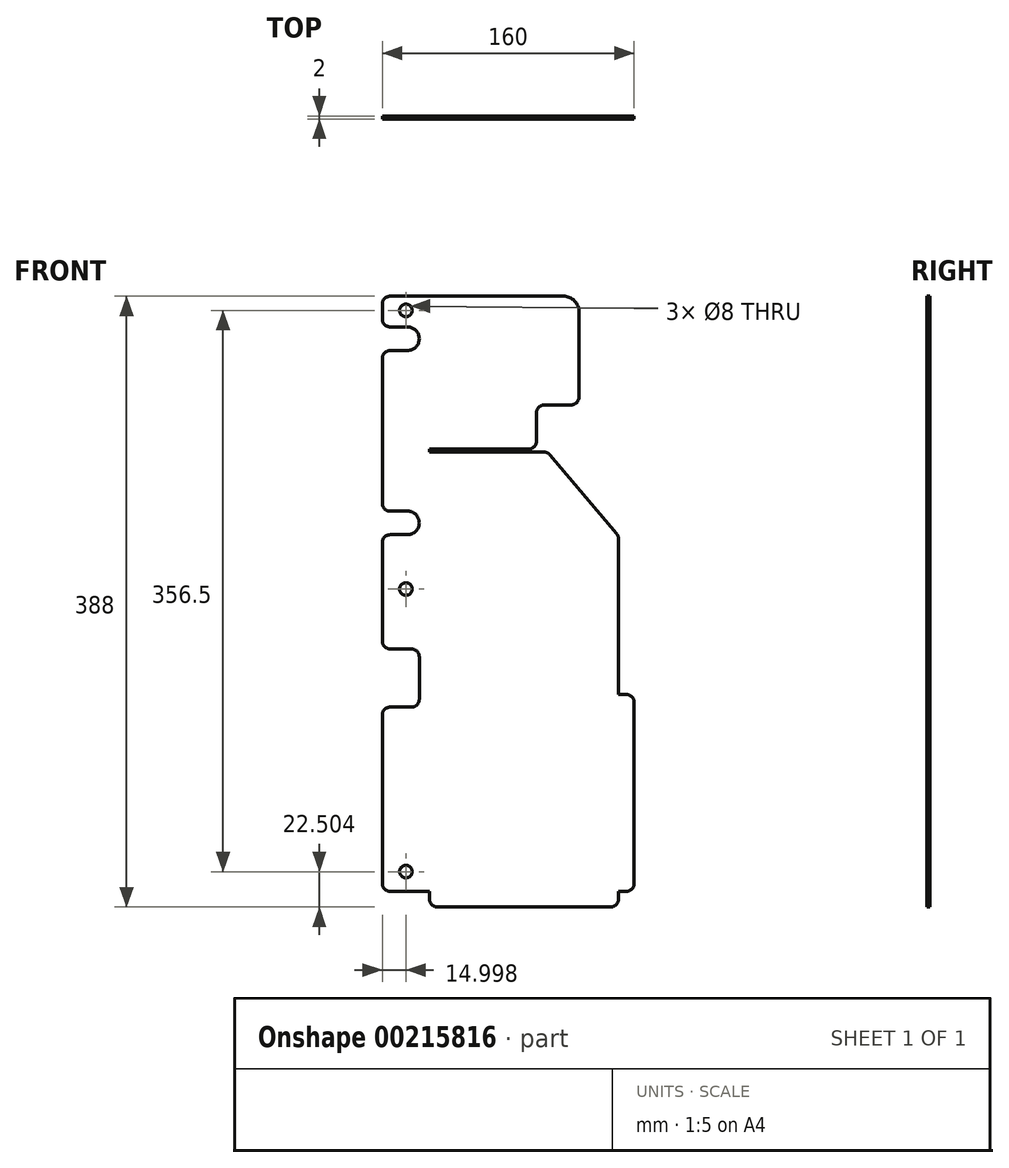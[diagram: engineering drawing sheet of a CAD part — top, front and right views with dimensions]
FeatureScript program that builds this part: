
annotation { "Feature Type Name" : "Feature", "Feature Type Description" : "" }
export const myFeature = defineFeature(function(context is Context, id is Id, definition is map)
    precondition{}
    {
        {
            var Q0;
            Q0=qCreatedBy(makeId("Front.planeOp"),FACE);
            var sketch = newSketch(context, id + "F0", { "sketchPlane" : qUnion([Q0])});
            skLineSegment(sketch, "E0", {"start": v(-23.05, 148.62) * mm, "end": v(56.95, 148.62) * mm});
            skLineSegment(sketch, "E1", {"start": v(66.95, 138.62) * mm, "end": v(66.95, 84.64) * mm});
            skLineSegment(sketch, "E2", {"start": v(61.95, 79.64) * mm, "end": v(44.95, 79.64) * mm});
            skLineSegment(sketch, "E3", {"start": v(39.95, 74.64) * mm, "end": v(39.95, 56.62) * mm});
            skLineSegment(sketch, "E4", {"start": v(34.95, 51.62) * mm, "end": v(-28.05, 51.62) * mm});
            skLineSegment(sketch, "E5", {"start": v(-28.05, 49.62) * mm, "end": v(44.63, 49.62) * mm});
            skLineSegment(sketch, "E6", {"start": v(48.45, 47.85) * mm, "end": v(90.76, -2.16) * mm});
            skLineSegment(sketch, "E7", {"start": v(91.95, -5.39) * mm, "end": v(91.95, -229.38) * mm});
            skLineSegment(sketch, "E8", {"start": v(91.95, -229.38) * mm, "end": v(-28.05, -229.38) * mm});
            skLineSegment(sketch, "E9", {"start": v(-28.05, -229.38) * mm, "end": v(-53.05, -229.38) * mm});
            skLineSegment(sketch, "E10", {"start": v(-58.05, -224.38) * mm, "end": v(-58.05, -117.38) * mm});
            skLineSegment(sketch, "E11", {"start": v(-53.05, 148.62) * mm, "end": v(-23.05, 148.62) * mm});
            skLineSegment(sketch, "E12", {"start": v(91.95, -104.38) * mm, "end": v(96.95, -104.38) * mm});
            skLineSegment(sketch, "E13", {"start": v(101.95, -109.38) * mm, "end": v(101.95, -224.38) * mm});
            skLineSegment(sketch, "E14", {"start": v(96.95, -229.38) * mm, "end": v(91.95, -229.38) * mm});
            skLineSegment(sketch, "E15", {"start": v(91.95, -229.38) * mm, "end": v(91.95, -234.38) * mm});
            skLineSegment(sketch, "E16", {"start": v(86.95, -239.38) * mm, "end": v(-23.05, -239.38) * mm});
            skLineSegment(sketch, "E17", {"start": v(-28.05, -234.38) * mm, "end": v(-28.05, -229.38) * mm});
            skLineSegment(sketch, "E18", {"start": v(-53.05, -75.38) * mm, "end": v(-39.55, -75.38) * mm});
            skLineSegment(sketch, "E19", {"start": v(-53.05, -112.38) * mm, "end": v(-39.55, -112.38) * mm});
            skLineSegment(sketch, "E20.trimOffspring", {"start": v(-58.05, -70.38) * mm, "end": v(-58.05, -7.87) * mm});
            skPoint(sketch, "E21.newPointA", {"position": v(-28.05, -75.38) * mm});
            skPoint(sketch, "E21.newPointB", {"position": v(-28.05, 148.62) * mm});
            skPoint(sketch, "E22.newPointA", {"position": v(-28.05, -229.38) * mm});
            skPoint(sketch, "E23.visualSharp", {"position": v(-58.05, -112.38) * mm});
            skArc(sketch, "E23.filletArc", {"start": v(-53.05, -112.38) * mm, "mid": v(-56.59, -113.84) * mm, "end": v(-58.05, -117.38) * mm});
            skPoint(sketch, "E24.visualSharp", {"position": v(-58.05, -75.38) * mm});
            skArc(sketch, "E24.filletArc", {"start": v(-58.05, -70.38) * mm, "mid": v(-56.59, -73.91) * mm, "end": v(-53.05, -75.38) * mm});
            skPoint(sketch, "E25.visualSharp", {"position": v(-58.05, 148.62) * mm});
            skArc(sketch, "E25.filletArc", {"start": v(-53.05, 148.62) * mm, "mid": v(-56.59, 147.16) * mm, "end": v(-58.05, 143.62) * mm});
            skPoint(sketch, "E26.visualSharp", {"position": v(66.95, 148.62) * mm});
            skArc(sketch, "E26.filletArc", {"start": v(66.95, 138.62) * mm, "mid": v(64.02, 145.7) * mm, "end": v(56.95, 148.62) * mm});
            skPoint(sketch, "E27.visualSharp", {"position": v(66.95, 79.64) * mm});
            skArc(sketch, "E27.filletArc", {"start": v(61.95, 79.64) * mm, "mid": v(65.48, 81.1) * mm, "end": v(66.95, 84.64) * mm});
            skPoint(sketch, "E28.visualSharp", {"position": v(39.95, 79.64) * mm});
            skArc(sketch, "E28.filletArc", {"start": v(44.95, 79.64) * mm, "mid": v(41.41, 78.17) * mm, "end": v(39.95, 74.64) * mm});
            skPoint(sketch, "E29.visualSharp", {"position": v(39.95, 51.62) * mm});
            skArc(sketch, "E29.filletArc", {"start": v(34.95, 51.62) * mm, "mid": v(38.48, 53.09) * mm, "end": v(39.95, 56.62) * mm});
            skPoint(sketch, "E30.visualSharp", {"position": v(46.95, 49.62) * mm});
            skArc(sketch, "E30.filletArc", {"start": v(48.45, 47.85) * mm, "mid": v(46.73, 49.16) * mm, "end": v(44.63, 49.62) * mm});
            skPoint(sketch, "E31.visualSharp", {"position": v(91.95, -3.55) * mm});
            skArc(sketch, "E31.filletArc", {"start": v(91.95, -5.39) * mm, "mid": v(91.64, -3.67) * mm, "end": v(90.76, -2.16) * mm});
            skPoint(sketch, "E32.visualSharp", {"position": v(101.95, -104.38) * mm});
            skArc(sketch, "E32.filletArc", {"start": v(101.95, -109.38) * mm, "mid": v(100.48, -105.84) * mm, "end": v(96.95, -104.38) * mm});
            skPoint(sketch, "E33.visualSharp", {"position": v(101.95, -229.38) * mm});
            skArc(sketch, "E33.filletArc", {"start": v(96.95, -229.38) * mm, "mid": v(100.48, -227.91) * mm, "end": v(101.95, -224.38) * mm});
            skPoint(sketch, "E34.visualSharp", {"position": v(91.95, -239.38) * mm});
            skArc(sketch, "E34.filletArc", {"start": v(86.95, -239.38) * mm, "mid": v(90.48, -237.91) * mm, "end": v(91.95, -234.38) * mm});
            skPoint(sketch, "E35.visualSharp", {"position": v(-28.05, -239.38) * mm});
            skArc(sketch, "E35.filletArc", {"start": v(-28.05, -234.38) * mm, "mid": v(-26.59, -237.91) * mm, "end": v(-23.05, -239.38) * mm});
            skPoint(sketch, "E36.visualSharp", {"position": v(-58.05, -229.38) * mm});
            skArc(sketch, "E36.filletArc", {"start": v(-58.05, -224.38) * mm, "mid": v(-56.59, -227.91) * mm, "end": v(-53.05, -229.38) * mm});
            skCircle(sketch, "E37", {"center": v(-43.05, 139.62) * mm, "radius": 4 * mm});
            skArc(sketch, "E38", {"start": v(-42.05, 114.12) * mm, "mid": v(-34.55, 121.62) * mm, "end": v(-42.05, 129.12) * mm});
            skLineSegment(sketch, "E39", {"start": v(-42.05, 114.12) * mm, "end": v(-53.05, 114.12) * mm});
            skLineSegment(sketch, "E40", {"start": v(-42.05, 129.12) * mm, "end": v(-53.05, 129.12) * mm});
            skPoint(sketch, "E41.visualSharp", {"position": v(-58.05, 129.12) * mm});
            skArc(sketch, "E41.filletArc", {"start": v(-58.05, 134.12) * mm, "mid": v(-56.59, 130.59) * mm, "end": v(-53.05, 129.12) * mm});
            skPoint(sketch, "E42.visualSharp", {"position": v(-58.05, 114.12) * mm});
            skArc(sketch, "E42.filletArc", {"start": v(-53.05, 114.12) * mm, "mid": v(-56.59, 112.66) * mm, "end": v(-58.05, 109.12) * mm});
            skArc(sketch, "E43", {"start": v(-42.33, -2.87) * mm, "mid": v(-34.55, 4.5) * mm, "end": v(-42.08, 12.12) * mm});
            skLineSegment(sketch, "E44", {"start": v(-42.33, -2.87) * mm, "end": v(-53.05, -2.87) * mm});
            skLineSegment(sketch, "E45", {"start": v(-42.02, 12.12) * mm, "end": v(-53.05, 12.12) * mm});
            skLineSegment(sketch, "E46.trimOffspring", {"start": v(-58.05, 17.12) * mm, "end": v(-58.05, 109.12) * mm});
            skPoint(sketch, "E47.visualSharp", {"position": v(-58.05, 12.12) * mm});
            skArc(sketch, "E47.filletArc", {"start": v(-58.05, 17.12) * mm, "mid": v(-56.59, 13.59) * mm, "end": v(-53.05, 12.12) * mm});
            skPoint(sketch, "E48.visualSharp", {"position": v(-58.05, -2.87) * mm});
            skArc(sketch, "E48.filletArc", {"start": v(-53.05, -2.87) * mm, "mid": v(-56.59, -4.34) * mm, "end": v(-58.05, -7.87) * mm});
            skCircle(sketch, "E49", {"center": v(-43.05, -37.38) * mm, "radius": 4 * mm});
            skCircle(sketch, "E50", {"center": v(-43.05, -216.88) * mm, "radius": 4 * mm});
            skLineSegment(sketch, "E51", {"start": v(-34.55, -80.38) * mm, "end": v(-34.55, -107.38) * mm});
            skPoint(sketch, "E52.visualSharp", {"position": v(-34.55, -75.38) * mm});
            skArc(sketch, "E52.filletArc", {"start": v(-34.55, -80.38) * mm, "mid": v(-36.02, -76.84) * mm, "end": v(-39.55, -75.38) * mm});
            skPoint(sketch, "E53.visualSharp", {"position": v(-34.55, -112.38) * mm});
            skArc(sketch, "E53.filletArc", {"start": v(-39.55, -112.38) * mm, "mid": v(-36.02, -110.91) * mm, "end": v(-34.55, -107.38) * mm});
            skLineSegment(sketch, "E54", {"start": v(-28.05, 49.62) * mm, "end": v(-28.05, 51.62) * mm});
            skLineSegment(sketch, "E55.trimOffspring", {"start": v(-58.05, 109.12) * mm, "end": v(-58.05, 17.12) * mm});
            skLineSegment(sketch, "E56.trimOffspring", {"start": v(-58.05, 134.12) * mm, "end": v(-58.05, 143.62) * mm});
            skLineSegment(sketch, "E57.trimOffspring", {"start": v(-58.05, -7.87) * mm, "end": v(-58.05, -70.38) * mm});
            skSolve(sketch);
        }
        {
            var Q0;
            Q0=makeQuery(id+"F0.imprint","IMPRINT",FACE,{"disambiguationData":[TD([[makeQuery(id+"F0.imprint","IMPRINT",EDGE,{"derivedFrom":sQuery(id+"F0.wireOp",EDGE,"E0")}),-1.0]])]});
            var Q1;
            Q1=makeQuery(id+"F0.imprint","IMPRINT",FACE,{"disambiguationData":[TD([[makeQuery(id+"F0.imprint","IMPRINT",EDGE,{"derivedFrom":sQuery(id+"F0.wireOp",EDGE,"E8")}),1.0]])]});
            var Q2;
            {var subQ1=sQuery(id+"F0.wireOp",EDGE,"E12");Q2=makeQuery(id+"F0.imprint","IMPRINT",FACE,{"disambiguationData":[TD([[makeQuery(id+"F0.imprint","IMPRINT",EDGE,{"derivedFrom":subQ1}),-1.0]])]});}
            extrude(context, id + "F1", {"entities" : qUnion([Q0, Q1, Q2]), "depth" : 2 * mm});
        }
    });
